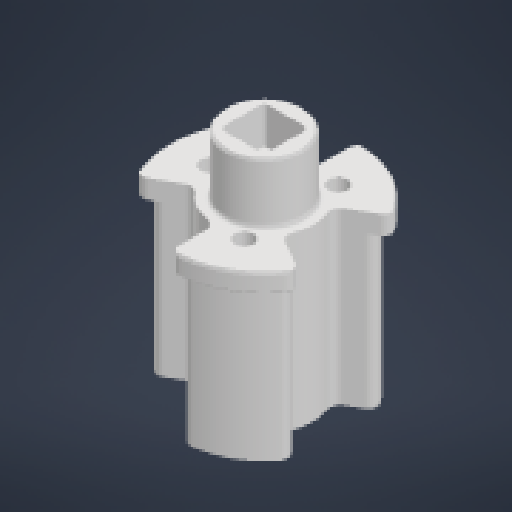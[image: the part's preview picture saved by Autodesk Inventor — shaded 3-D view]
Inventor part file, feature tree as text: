
AUTODESK INVENTOR PART (.ipt)
format: ipt  version: 2024 (Build 280153000, 153)  size: 283,648 bytes
history: native  units: in
note: dims shown in document units (in); Inventor stores cm internally (conversion verified against a paired STEP export)
features: extrude x1, sketch x1
ambient origin geometry x8: Origin, YZ Plane, XZ Plane, XY Plane, X Axis, Y Axis, Z Axis, Center Point
bodies: Solid2 (feature_tree), Solid1 (feature_tree)
feature tree (2):
  extrude  "Extrusion1"  [1 undecoded]
  sketch  "Sketch1"  dims[d0=0.205in d1=0.55in d2=0.0in d3=0.0in]
note: 1 required parameter value undecoded (feature->parameter linkage not recoverable at this tier; creation-order binding heuristic only, values carry confidence <= 0.55)
